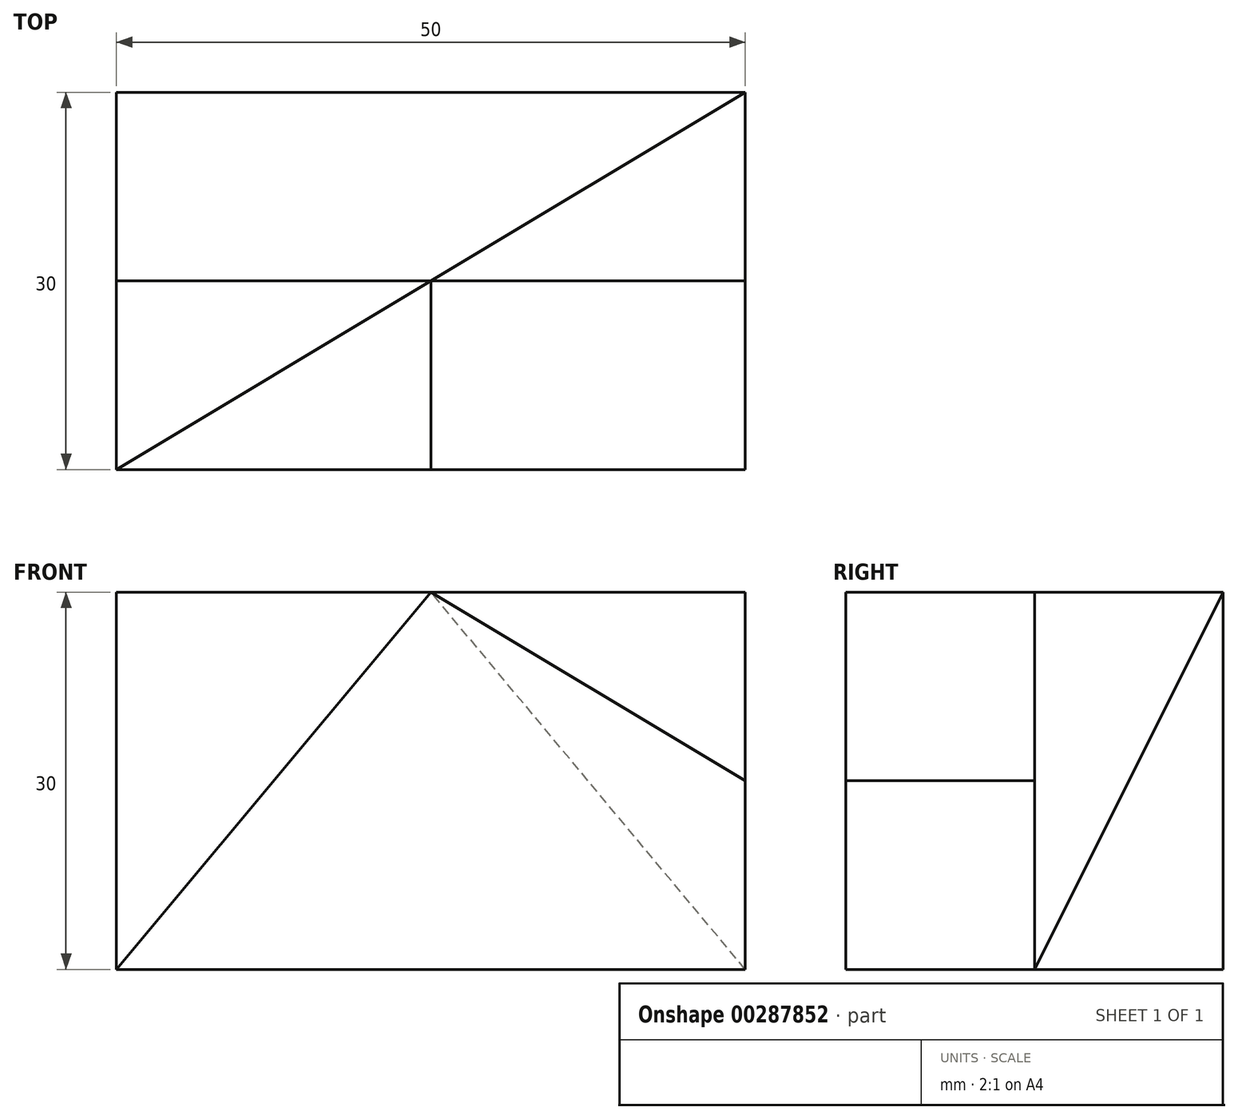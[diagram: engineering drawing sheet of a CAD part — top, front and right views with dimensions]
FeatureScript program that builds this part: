
annotation { "Feature Type Name" : "Feature", "Feature Type Description" : "" }
export const myFeature = defineFeature(function(context is Context, id is Id, definition is map)
    precondition{}
    {
        {
            var Q0;
            Q0=qCreatedBy(makeId("Right.planeOp"),FACE);
            var sketch = newSketch(context, id + "F0", { "sketchPlane" : qUnion([Q0])});
            skLineSegment(sketch, "E0.bottom", {"start": v(0, 0) * mm, "end": v(30, 0) * mm});
            skLineSegment(sketch, "E0.top", {"start": v(0, 30) * mm, "end": v(30, 30) * mm});
            skLineSegment(sketch, "E0.left", {"start": v(0, 0) * mm, "end": v(0, 30) * mm});
            skLineSegment(sketch, "E0.right", {"start": v(30, 0) * mm, "end": v(30, 30) * mm});
            skLineSegment(sketch, "E1", {"start": v(15, 30) * mm, "end": v(0, 0) * mm});
            skLineSegment(sketch, "E2", {"start": v(15, 30) * mm, "end": v(15, 0) * mm});
            skSolve(sketch);
        }
        {
            var Q0;
            {var subQ0=sQuery(id+"F0.wireOp",EDGE,"E0.right");Q0=makeQuery(id+"F0.imprint","IMPRINT",FACE,{"disambiguationData":[TD([[makeQuery(id+"F0.imprint","IMPRINT",EDGE,{"derivedFrom":subQ0}),1.0]])]});}
            var Q1;
            {var subQ0=sQuery(id+"F0.wireOp",EDGE,"E1");Q1=makeQuery(id+"F0.imprint","IMPRINT",FACE,{"disambiguationData":[TD([[makeQuery(id+"F0.imprint","IMPRINT",EDGE,{"derivedFrom":subQ0}),1.0]])]});}
            extrude(context, id + "F1", {"entities" : qUnion([Q0, Q1]), "depth" : 25 * mm});
        }
        {
            var Q0;
            {var subQ0=sQuery(id+"F0.wireOp",EDGE,"E0.right");Q0=makeQuery(id+"F0.imprint","IMPRINT",FACE,{"disambiguationData":[TD([[makeQuery(id+"F0.imprint","IMPRINT",EDGE,{"derivedFrom":subQ0}),1.0]])]});}
            extrude(context, id + "F2", {"entities" : qUnion([Q0]), "operationType" : NewBodyOperationType.ADD, "depth" : 50 * mm});
        }
        {
            var Q0;
            Q0=makeQuery(id+"F2.opExtrude","CAP_VERTEX",VERTEX,{"disambiguationData":[OSD([sQuery(id+"F0.wireOp",EDGE,"E0.top"),sQuery(id+"F0.wireOp",EDGE,"E0.right")])],"isStart":false});
            var Q1;
            Q1=makeQuery(id+"F1.opExtrude","CAP_VERTEX",VERTEX,{"disambiguationData":[OSD([sQuery(id+"F0.wireOp",EDGE,"E0.top"),sQuery(id+"F0.wireOp",EDGE,"E1"),sQuery(id+"F0.wireOp",EDGE,"E2")])],"isStart":false});
            var Q2;
            Q2=makeQuery(id+"F2.opExtrude","CAP_VERTEX",VERTEX,{"disambiguationData":[OSD([sQuery(id+"F0.wireOp",EDGE,"E0.bottom"),sQuery(id+"F0.wireOp",EDGE,"E2")])],"isStart":false});
            cPlane(context, id + "F3", {"entities" : qUnion([Q0, Q1, Q2]), "cplaneType" : CPlaneType.THREE_POINT, "offset" : 25 * mm, "width" : 150 * mm, "height" : 150 * mm});
        }
        {
            var Q0;
            Q0=qCreatedBy(id+"F3.planeOp",FACE);
            var sketch = newSketch(context, id + "F4", { "sketchPlane" : qUnion([Q0])});
            skPoint(sketch, "E3.0", {"position": v(-50.4, 40.25) * mm});
            skPoint(sketch, "E4.0", {"position": v(-22.03, 33.54) * mm});
            skPoint(sketch, "E5.0", {"position": v(-50.4, 6.7) * mm});
            skLineSegment(sketch, "E6", {"start": v(-22.03, 33.54) * mm, "end": v(-50.4, 40.25) * mm});
            skLineSegment(sketch, "E7", {"start": v(-50.4, 40.25) * mm, "end": v(-50.4, 6.7) * mm});
            skLineSegment(sketch, "E8", {"start": v(-50.4, 6.7) * mm, "end": v(-22.03, 33.54) * mm});
            skSolve(sketch);
        }
        {
            var Q0;
            Q0 = qSketchRegion(id + "F4", true);
            extrude(context, id + "F5", {"entities" : qUnion([Q0]), "operationType" : NewBodyOperationType.REMOVE, "endBound" : BoundingType.THROUGH_ALL, "oppositeDirection" : true, "depth" : 25 * mm});
        }
        {
            var Q0;
            Q0=qCreatedBy(makeId("Front.planeOp"),FACE);
            var sketch = newSketch(context, id + "F6", { "sketchPlane" : qUnion([Q0])});
            skLineSegment(sketch, "E9.0", {"start": v(50, 0) * mm, "end": v(25, 0) * mm});
            skLineSegment(sketch, "E10.0", {"start": v(25, 0) * mm, "end": v(0, 0) * mm});
            skLineSegment(sketch, "E11.0", {"start": v(50, 15) * mm, "end": v(50, 0) * mm});
            skLineSegment(sketch, "E12", {"start": v(0, 0) * mm, "end": v(25, 30) * mm});
            skLineSegment(sketch, "E13", {"start": v(25, 30) * mm, "end": v(50, 15) * mm});
            skPoint(sketch, "E14.orphan", {"position": v(50, 30) * mm});
            skSolve(sketch);
        }
        {
            var Q0;
            Q0 = qSketchRegion(id + "F6", true);
            extrude(context, id + "F7", {"entities" : qUnion([Q0]), "operationType" : NewBodyOperationType.ADD, "oppositeDirection" : true, "depth" : 15 * mm});
        }
    });
